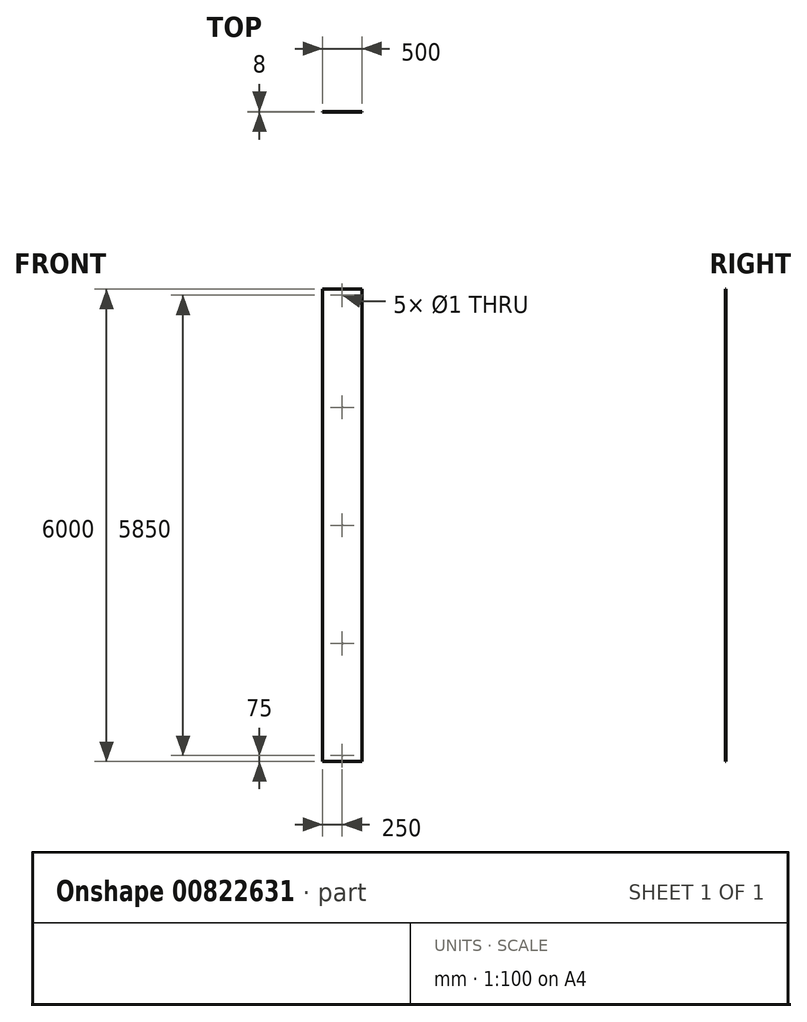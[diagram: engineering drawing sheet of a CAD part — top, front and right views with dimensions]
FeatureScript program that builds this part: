
annotation { "Feature Type Name" : "Feature", "Feature Type Description" : "" }
export const myFeature = defineFeature(function(context is Context, id is Id, definition is map)
    precondition{}
    {
        {
            var Q0;
            Q0=qCreatedBy(makeId("Front.planeOp"),FACE);
            var sketch = newSketch(context, id + "F0", { "sketchPlane" : qUnion([Q0])});
            skLineSegment(sketch, "E0.bottom", {"start": v(-250, 3000) * mm, "end": v(250, 3000) * mm});
            skLineSegment(sketch, "E0.top", {"start": v(-250, -3000) * mm, "end": v(250, -3000) * mm});
            skLineSegment(sketch, "E0.left", {"start": v(-250, 3000) * mm, "end": v(-250, -3000) * mm});
            skLineSegment(sketch, "E0.right", {"start": v(250, 3000) * mm, "end": v(250, -3000) * mm});
            skPoint(sketch, "E0.middle", {"position": v(0, 0) * mm});
            skSolve(sketch);
        }
        {
            var Q0;
            Q0=makeQuery(id+"F0.imprint","IMPRINT",FACE,{"disambiguationData":[TD([[makeQuery(id+"F0.imprint","IMPRINT",EDGE,{"derivedFrom":sQuery(id+"F0.wireOp",EDGE,"E0.bottom")}),-1.0]])]});
            extrude(context, id + "F1", {"entities" : qUnion([Q0]), "depth" : 8 * mm, "offsetDistance" : 25 * mm, "symmetric" : true});
        }
        {
            var Q0;
            Q0=makeQuery(id+"F1.opExtrude","CAP_FACE",FACE,{"disambiguationData":[OSD([sQuery(id+"F0.wireOp",EDGE,"E0.bottom"),sQuery(id+"F0.wireOp",EDGE,"E0.top"),sQuery(id+"F0.wireOp",EDGE,"E0.left"),sQuery(id+"F0.wireOp",EDGE,"E0.right")])],"isStart":false});
            var sketch = newSketch(context, id + "F2", { "sketchPlane" : qUnion([Q0])});
            skLineSegment(sketch, "E1", {"start": v(250, 0) * mm, "end": v(-250, 0) * mm});
            skLineSegment(sketch, "E2", {"start": v(0, 0) * mm, "end": v(0, -1500) * mm});
            skLineSegment(sketch, "E3", {"start": v(0, -1500) * mm, "end": v(0, -2925) * mm});
            skLineSegment(sketch, "E4", {"start": v(0, 0) * mm, "end": v(0, 1500) * mm});
            skLineSegment(sketch, "E5", {"start": v(0, 1500) * mm, "end": v(0, 2925) * mm});
            skPoint(sketch, "E6", {"position": v(0, 2925) * mm});
            skPoint(sketch, "E7", {"position": v(0, 1500) * mm});
            skPoint(sketch, "E8", {"position": v(0, 0) * mm});
            skPoint(sketch, "E9", {"position": v(0, -1500) * mm});
            skPoint(sketch, "E10", {"position": v(0, -2925) * mm});
            skSolve(sketch);
        }
        {
            var Q0;
            Q0=sQuery(id+"F2.wireOp",VERTEX,"E6");
            var Q1;
            Q1=sQuery(id+"F2.wireOp",VERTEX,"E7");
            var Q2;
            Q2=sQuery(id+"F2.wireOp",VERTEX,"E8");
            var Q3;
            Q3=sQuery(id+"F2.wireOp",VERTEX,"E9");
            var Q4;
            Q4=sQuery(id+"F2.wireOp",VERTEX,"E10");
            var Q5;
            Q5=makeQuery(id+"F1.opExtrude","SWEPT_BODY",BODY,{"disambiguationData":[OSD([sQuery(id+"F0.wireOp",EDGE,"E0.bottom"),sQuery(id+"F0.wireOp",EDGE,"E0.top"),sQuery(id+"F0.wireOp",EDGE,"E0.left"),sQuery(id+"F0.wireOp",EDGE,"E0.right")])]});
            hole(context, id + "F3", {"style" : HoleStyle.SIMPLE, "endStyle" : HoleEndStyle.THROUGH, "holeDiameter" : 1 * mm, "majorDiameter" : 5 * mm, "isTappedThrough" : true, "tappedDepth" : 12 * mm, "tapClearance" : 3, "locations" : qUnion([Q0, Q1, Q2, Q3, Q4]), "scope" : qUnion([Q5])});
        }
    });
